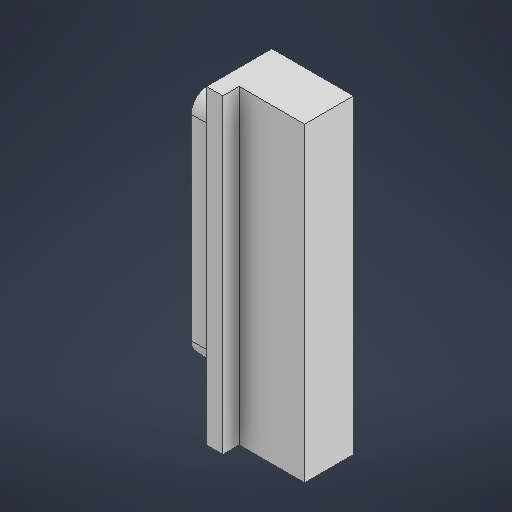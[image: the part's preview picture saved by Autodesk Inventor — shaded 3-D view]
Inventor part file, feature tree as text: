
AUTODESK INVENTOR PART (.ipt)
format: ipt  version: 2025 (Build 290162000, 162)  size: 204,800 bytes
history: native  units: mm
features: extrude x3, sketch x3
ambient origin geometry x8: Origin, YZ Plane, XZ Plane, XY Plane, X Axis, Y Axis, Z Axis, Center Point
bodies: 实体1 (feature_tree)
feature tree (6):
  extrude  "拉伸1"  Depth=19.0mm
  extrude  "拉伸2"  Depth=1.0mm
  extrude  "拉伸3"  Depth=2.0mm
  sketch  "草图1"  dims[d0=5.0mm d1=19.0mm]
  sketch  "草图2"  dims[d2=3.0mm d3=0.0mm d4=1.0mm]
  sketch  "草图3"  dims[d5=1.0mm d6=0.0mm d7=2.0mm d8=14.0mm d9=3.0mm d10=3.0mm d11=0.0mm]
